# Revit family: IS_Connect_E5039_BIM_DE
name_source: partatom
category: Plumbing Fixtures
revit_build: Autodesk Revit MEP 2016 (Build: 20161004_0715(x64)
units: mm (PartAtom-declared; Revit-internal decimal feet)

## family parameters
Always vertical = No
Cut with Voids When Loaded = No
OmniClass Number = 23.45.05.14.14
OmniClass Title = Sinks/Lavatories
Part Type = Normal
Room Calculation Point = No
Round Connector Dimension = Use Diameter
Shared = No
Work Plane-Based = No

## types (2) — shared parameters
Accessories = www.idealstandard.de\ersatzteile
AreaUnits = millimeters
Assembly Code = C1030203
AssetType = Fixed
BIMObjectName = ISI_IdealStandard_Sinks_CONNECT_E503901
BOSUseNativeGeometries = 1
BarCode = 5017830446736
Brand url = http://www.idealstandard.co.uk
CodePerformance = DIN EN 14688 CL 15, DIN EN 31
Color = White
ConnectionType = Plumbing
CurrencyUnit = €
Description = CONNECT countertop washbasin 550x430mm, 1 taphole, with overflow
DurationUnit = year
EAN code = https://5017830446736
Edition number = 1
ExpectedLife = 25
Features = CONNECT countertop washbasin 550x430mm, 1 taphole, with overflow
Finish = White
GrossWeight = 9,45 kg
Installation instructions = http://www.idealstandard.de
InstallationDate = 1900-12-31T23:59:59
InstallationInstructions = www.idealstandard.de\produkte
LinearUnits = millimeters
Manufacturer name = Ideal Standard
ManufacturerURL = www.idealstandard.de
Material = Vitreous china
Material main = Ceramics
ModelReference = IS Einbauwaschtisch CONNECT, oval, 1Hl., m.Ül., 550x430x175mm, Weiß
Nominal height = 175
Nominal width = 550
NominalLength = 430 mm
Product Guid = 95b64dd1-543b-4c65-b836-e5c1ea6d9aef
Product SKU = E5039
Product data url = https://bimobject.com
Product family = CONNECT
Product group = Basin
Product url = http://www.idealstandard.de
ProductInformation = www.idealstandard.de
QR code = http://bimobject.com
Shape = Sculptured
Size = 540 x 430 x 202 mm
Space = Internal
Technical description = http://www.idealstandard.de
URL = www.idealstandard.de
Uniclass2015Code = Pr_40_20_96_81
Uniclass2015Title = Sinks
Uniclass2015Version = Products v1.1
Version = 1
VolumeUnits = Litres
Weight Net (Kg) = 8.45
zero-valued in all types: Cost, NominalDepth, ProfonditaNominale

## per-type parameters (varying)
| type | Model | ModelNumber | Name |
| E503901 CONNECT countertop washbasin 550x430mm, 1 taphole, with overflow | E503901 | E503901 | ISI_IdealStandard_Sinks_CONNECT_E503901 |
| E5039MA CONNECT countertop washbasin 550x430mm, 1 taphole, with overflow with Ideal Plus | E5039MA | E5039MA | ISI_IdealStandard_Sinks_CONNECT_E5039MA |

## geometry (parser evidence)
native form markers: Blend x2, Sweep x3
no freeform markers — native parametric forms only
